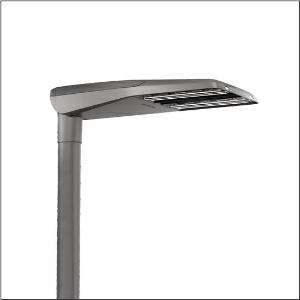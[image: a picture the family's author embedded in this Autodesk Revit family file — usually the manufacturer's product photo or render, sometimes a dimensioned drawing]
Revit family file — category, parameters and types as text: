
# Revit family: streetlight_sl_11_iq_midi___st1_2a_5xc3a61f08me_e1b3
name_source: partatom
category: Lighting Fixtures
units: mm (PartAtom-declared; Revit-internal decimal feet)

## family parameters
Cut with Voids When Loaded = No
Host = Face
Light Source = No
Part Type = Normal
Room Calculation Point = No
Round Connector Dimension = Use Diameter
Shared = No

## types (1)
- --- (1 x LED, 16120 lm, 123.9 W, 2700K)
    Apparent Load = 124 VA
    CIE Flux Codes = 32 70 96 100 100
    Color Rendering = 70
    Color Temperature = 2700K
    Default Elevation = 1800 mm
    Description = Streetlight SL 11 iQ midi, mast luminaire, primary light control with 3 zone facetted reflector, of plastic, silver coated, highly specular, primary optical cover: cover, of PMMA, transparent, light distribution: ST1.2a, light emission: direct distribution, primary light characteristic: asymmetric, installation type: post-top, side-entry, LED, High Power LED, rated luminous flux: 16.120lm, luminous efficacy: 130lm/W, light colour: 727, colour temperature: 2700K, control: Street-Remote, Auto-Match, Temp-Guard, Lumen-Switch, Night-Set, Smart-Wire, Light-Fading, Desk-Remote (wireless, voltage-free reading and setting of iQ features in the workshop via application-optimized NFC function/RFID function), optimised constant luminous flux control (CLO 2.0), with cable H07RN-F 5x 1.5mm², mains connection: 230..240V, AC, 50/60Hz, connection cable pre-assembled, cable length: 12,5m, start of lifetime: 124W, end of service life: 131W, reduction: 57W, luminaire housing, of diecast aluminium, powder-coated, Siteco® metallic grey (DB 702S), please order mast flange separately, inclination adjustable without tools: 0°, 5°, 10°, 15° (post-top) | 0°, -5°, -10°, -15° (side-entry), sealing non-destructively replaceable, multi-level sealing system, length: 780mm, width: 376mm, height: 118mm, mast flange for spigot size: 42mm (side-entry): 5XC10008XM4, 60/48mm (side-entry/post-top): 5XC10108XM2, 76/60mm (side-entry/post-top): 5XC10108XM1, equipment: Power, protection rating (complete): IP66, insulation class (complete): insulation class II (safety insulation), certification: CE, ENEC, VDE, impact resistance: IK09, permissible operating ambient temperature for outdoor applications: -25..+50°C, standard-compliant lighting for roads and squares, Environmental Product Declaration (EPD) tested and certified by an independent institute, packaging unit: 1 piece

Light Distribution: ST1.2a
    Height = 118 mm
    Lamp = 1 x LED
    Lamp Light Flux = 16120 lm
    Lamp Power = 123.9 W
    Lamp count = 1
    Length = 780 mm
    Luminous efficacy = 130 lm/W
    Manufacturer = Siteco
    ModVariant = No
    Model = 5XC3A61F08ME
    Number of Poles = 1
    OnlyDefault = Yes
    Power Factor = 1
    Product Name = Streetlight SL 11 iQ midi | ST1.2a
    Product group = mast luminaire | pylon top
    ProductGroupID = 6100
    Protection Class = Protection class II
    Protection Degree = IP 66
    RLX_Detail_Level = 1
    RLX_Emergency_Light_Flux = 0 lm
    RLX_Emergency_Type = 0
    RLX_Emergency_Type_DB = No
    RlxData = <blob elided: 70777 chars, md5=48bd36f7>
    Socket = socket
    Standby Power = 0 W
    System Light Flux = 16119 lm
    System Power = 124 W
    Type Comments = factory setting: luminous flux: 100 % | dim-lin: 254 | 554 mA
    Type Image = l_1005960.jpg
    URL = http://relux.com
    VarID = @adj_029329
    Voltage = 0 V
    Weight = 0.00 kg
    Width = 376 mm

## geometry (parser evidence)
native form markers: Blend x4, Sweep x10
no freeform markers — native parametric forms only
